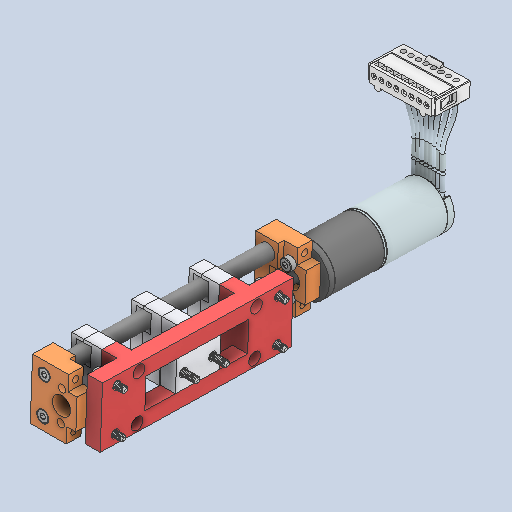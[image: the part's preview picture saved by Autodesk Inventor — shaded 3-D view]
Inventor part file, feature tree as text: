
AUTODESK INVENTOR PART (.ipt)
format: ipt  version: 2023 (Build 270158000, 158)  size: 16,023,040 bytes
history: native  units: mm
features: other x43, sketch x1
ambient origin geometry x8: Origin, YZ Plane, XZ Plane, XY Plane, X Axis, Y Axis, Z Axis, Center Point
bodies: Solid1 (feature_tree), Solid4 (feature_tree), Solid5 (feature_tree), Solid6 (feature_tree), Solid7 (feature_tree), Solid8 (feature_tree), Solid9 (feature_tree), Solid10 (feature_tree), Solid11 (feature_tree), Solid12 (feature_tree), Solid13 (feature_tree), Solid14 (feature_tree), Solid15 (feature_tree), Solid16 (feature_tree), Solid17 (feature_tree), Solid18 (feature_tree), Solid19 (feature_tree), Solid20 (feature_tree), Solid21 (feature_tree), Solid22 (feature_tree), Solid23 (feature_tree), Solid24 (feature_tree), Solid25 (feature_tree), Solid26 (feature_tree), Solid27 (feature_tree), Solid28 (feature_tree), Solid29 (feature_tree), Solid30 (feature_tree), Solid31 (feature_tree), Solid32 (feature_tree), Solid33 (feature_tree), Solid34 (feature_tree), Solid35 (feature_tree), Solid36 (feature_tree), Solid37 (feature_tree), Solid38 (feature_tree), Solid39 (feature_tree), Solid40 (feature_tree), Solid41 (feature_tree), Solid42 (feature_tree), Solid43 (feature_tree), Solid44 (feature_tree), Solid45 (feature_tree), Solid46 (feature_tree), Solid2 (feature_tree), Solid3 (feature_tree)
feature tree (44):
  other  "Repaired Geometry1"
  sketch  "Sketch6"
  other  "Solid3:1"
  other  "Solid3:2"
  other  "Solid3:3"
  other  "Solid3:4"
  other  "Solid3:5"
  other  "Solid4:1"
  other  "Solid5:1"
  other  "Solid6:1"
  other  "Solid7:1"
  other  "Solid8:1"
  other  "Solid9:1"
  other  "Solid10:1"
  other  "Solid11:1"
  other  "Solid12:1"
  other  "Solid13:1"
  other  "Solid14:1"
  other  "Solid15:1"
  other  "Solid16:1"
  other  "Solid17:1"
  other  "Solid18:1"
  other  "Solid19:1"
  other  "Solid20:1"
  other  "Solid21:1"
  other  "Solid22:1"
  other  "Solid23:1"
  other  "Solid24:1"
  other  "Solid25:1"
  other  "Solid26:1"
  other  "Solid27:1"
  other  "Solid28:1"
  other  "Solid29:1"
  other  "Solid30:1"
  other  "Solid31:1"
  other  "Solid32:1"
  other  "Solid33:1"
  other  "Solid34:1"
  other  "Solid35:1"
  other  "Solid36:1"
  other  "Solid37:1"
  other  "Solid38:1"
  other  "Solid39:1"
  other  "Solid40:1"
